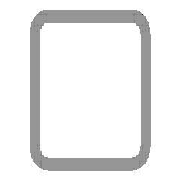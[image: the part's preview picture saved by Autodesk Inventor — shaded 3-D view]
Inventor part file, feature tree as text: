
AUTODESK INVENTOR PART (.ipt)
format: ipt  version: 2025 (Build 290162010, 162A)  size: 134,656 bytes
history: native  units: mm (DEFAULTED — no unit token found)
features: other x4, sketch x1, plane x1
ambient origin geometry x8: Origin, YZ Plane, XZ Plane, XY Plane, X Axis, Y Axis, Z Axis, Center Point
bodies: Solid1 (feature_tree), Body (feature_tree)
feature tree (6):
  parser-record x1  (decoder bookkeeping rows leaked as tree rows — omitted from the tree; the rows remain in map.json)
  other  "Driven Length"
  other  "Start plane"
  other  "End plane"
  sketch  "Sketch3"  dims[d3=2200.0mm d4=0.0mm d7=8.0mm d9=100.0mm d11=100.0mm d12=4.0mm d13=100.0mm d14=2300.0mm d15=50.0mm d16=50.0mm d17=90.0deg d18=2200.0mm]
  plane  "Work Plane3"
